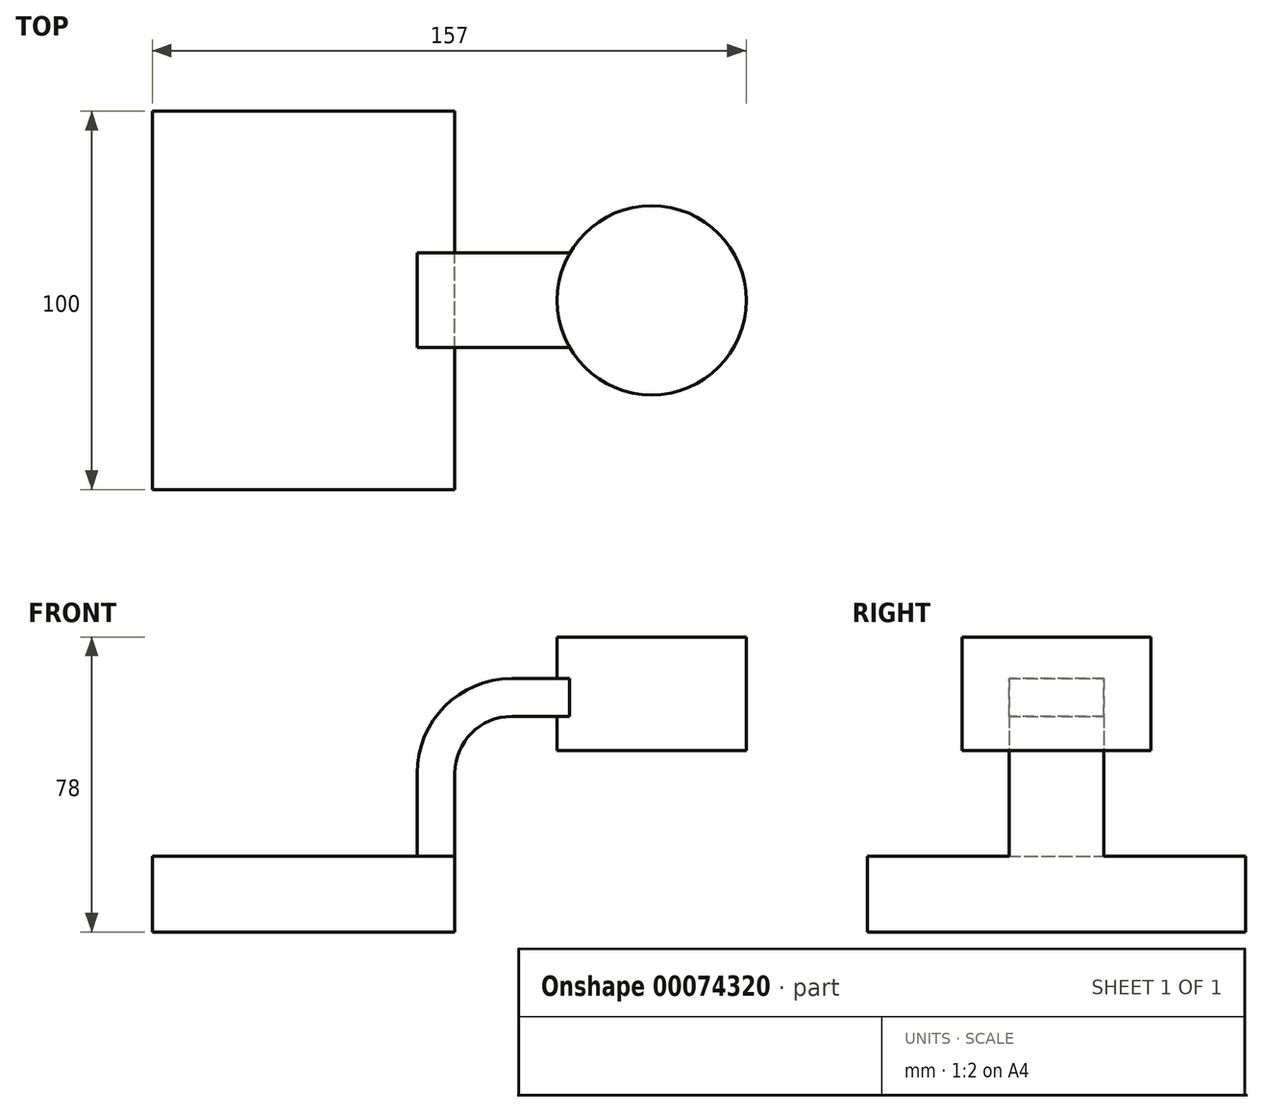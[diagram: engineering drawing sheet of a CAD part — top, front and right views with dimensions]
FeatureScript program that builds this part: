
annotation { "Feature Type Name" : "Feature", "Feature Type Description" : "" }
export const myFeature = defineFeature(function(context is Context, id is Id, definition is map)
    precondition{}
    {
        {
            var Q0;
            Q0=qCreatedBy(makeId("Front.planeOp"),FACE);
            var sketch = newSketch(context, id + "F0", { "sketchPlane" : qUnion([Q0])});
            skLineSegment(sketch, "E0.rect.bottom", {"start": v(40, -10) * mm, "end": v(-40, -10) * mm});
            skLineSegment(sketch, "E0.rect.top", {"start": v(40, 10) * mm, "end": v(-40, 10) * mm});
            skLineSegment(sketch, "E0.rect.left", {"start": v(40, -10) * mm, "end": v(40, 10) * mm});
            skLineSegment(sketch, "E0.rect.right", {"start": v(-40, -10) * mm, "end": v(-40, 10) * mm});
            skPoint(sketch, "E0.rect.middle", {"position": v(0, 0) * mm});
            skLineSegment(sketch, "E1.rect.bottom", {"start": v(117, 38) * mm, "end": v(67, 38) * mm});
            skLineSegment(sketch, "E1.rect.top", {"start": v(117, 68) * mm, "end": v(92, 68) * mm});
            skLineSegment(sketch, "E1.rect.left", {"start": v(117, 38) * mm, "end": v(117, 68) * mm});
            skLineSegment(sketch, "E1.rect.right", {"start": v(67, 38) * mm, "end": v(67, 68) * mm});
            skLineSegment(sketch, "E2", {"start": v(40, 10) * mm, "end": v(40, 32) * mm});
            skLineSegment(sketch, "E3", {"start": v(67, 47) * mm, "end": v(55, 47) * mm});
            skArc(sketch, "E4", {"start": v(40, 32) * mm, "mid": v(44.4, 42.6) * mm, "end": v(55, 47) * mm});
            skLineSegment(sketch, "E5.0", {"start": v(67, 57) * mm, "end": v(55, 57) * mm});
            skArc(sketch, "E5.1", {"start": v(30, 32) * mm, "mid": v(37.32, 49.68) * mm, "end": v(55, 57) * mm});
            skLineSegment(sketch, "E5.2", {"start": v(30, 9.66) * mm, "end": v(30, 32) * mm});
            skLineSegment(sketch, "E6", {"start": v(92, 57) * mm, "end": v(92, 47) * mm});
            skFitSpline(sketch, "E7", {"points": [v(-40, 10) * mm, v(67, 68) * mm], "startDerivative": vector(25.3, 91.18) * mm, "endDerivative": vector(168, -0.05) * mm});
            skLineSegment(sketch, "E8", {"start": v(92, 57) * mm, "end": v(92, 68) * mm});
            skLineSegment(sketch, "E9", {"start": v(92, 47) * mm, "end": v(92, 38) * mm});
            skPoint(sketch, "E9.endSnap0", {"position": v(92, 38) * mm});
            skLineSegment(sketch, "E10", {"start": v(67, 68) * mm, "end": v(92, 68) * mm});
            skSolve(sketch);
        }
        {
            var Q0;
            Q0=makeQuery(id+"F0.imprint","IMPRINT",FACE,{"disambiguationData":[TD([[makeQuery(id+"F0.imprint","IMPRINT",EDGE,{"derivedFrom":sQuery(id+"F0.wireOp",EDGE,"E0.rect.bottom")}),-1.0]])]});
            extrude(context, id + "F1", {"entities" : qUnion([Q0]), "endBound" : BoundingType.SYMMETRIC, "depth" : 100 * mm});
        }
        {
            var Q0;
            {var subQ5=sQuery(id+"F0.wireOp",EDGE,"E2");Q0=makeQuery(id+"F0.imprint","IMPRINT",FACE,{"disambiguationData":[TD([[makeQuery(id+"F0.imprint","IMPRINT",EDGE,{"derivedFrom":subQ5}),1.0]])]});}
            extrude(context, id + "F2", {"entities" : qUnion([Q0]), "operationType" : NewBodyOperationType.ADD, "endBound" : BoundingType.SYMMETRIC, "depth" : 25 * mm});
        }
        {
            var Q0;
            {var subQ4=sQuery(id+"F0.wireOp",EDGE,"E5.1");Q0=makeQuery(id+"F0.imprint","IMPRINT",FACE,{"disambiguationData":[TD([[makeQuery(id+"F0.imprint","IMPRINT",EDGE,{"derivedFrom":subQ4}),1.0]])]});}
            extrude(context, id + "F3", {"entities" : qUnion([Q0]), "operationType" : NewBodyOperationType.ADD, "endBound" : BoundingType.SYMMETRIC, "depth" : 10 * mm});
        }
        {
            var Q0;
            {var subQ0=sQuery(id+"F0.wireOp",EDGE,"E1.rect.left");Q0=makeQuery(id+"F0.imprint","IMPRINT",FACE,{"disambiguationData":[TD([[makeQuery(id+"F0.imprint","IMPRINT",EDGE,{"derivedFrom":subQ0}),1.0]])]});}
            var Q1;
            Q1=sQuery(id+"F0.wireOp",EDGE,"E6");
            revolve(context, id + "F4", {"operationType" : NewBodyOperationType.ADD, "entities" : qUnion([Q0]), "axis" : qUnion([Q1]), "revolveType" : RevolveType.FULL});
        }
        {
            var Q0;
            {var subQ0=sQuery(id+"F0.wireOp",EDGE,"E1.rect.right");Q0=makeQuery(id+"F3.boolean.opBoolean","MERGE",FACE,{"derivedFrom":[makeQuery(id+"F2.opExtrude","SWEPT_FACE",FACE,{"disambiguationData":[OSD([subQ0])]}),makeQuery(id+"F3.opExtrude","SWEPT_FACE",FACE,{"disambiguationData":[OSD([subQ0])]})]});}
            extrude(context, id + "F5", {"entities" : qUnion([Q0]), "operationType" : NewBodyOperationType.ADD, "depth" : 5 * mm});
        }
    });
